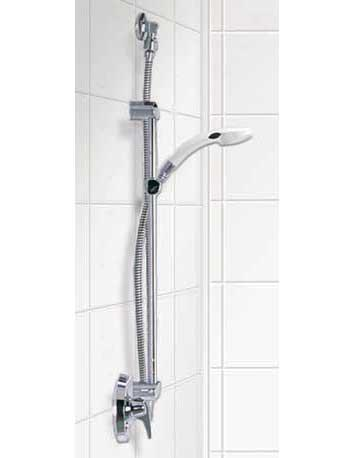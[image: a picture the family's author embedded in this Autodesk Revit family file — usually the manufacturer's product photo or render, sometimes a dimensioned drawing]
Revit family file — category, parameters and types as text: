
# Revit family: 13636FHARFR-L
name_source: partatom
category: Plumbing Fixtures
units: mm (PartAtom-declared; Revit-internal decimal feet)

## family parameters
Always vertical = Yes
Cut with Voids When Loaded = No
OmniClass Number = 23.45.00.00
OmniClass Title = Sanitary, Laundry, and Cleaning Equipment
Part Type = Normal
Room Calculation Point = No
Round Connector Dimension = Use Diameter
Shared = No
Work Plane-Based = No

## types (2) — shared parameters
Assembly Code = D2010710
Back Wall Thickness = 1 1/2"
Center of Shower = 19 1/4"
Default Elevation = 0"
Depth = 39 3/8"
Description = 62"W x 33"D COMPRESSION-MOLDED  SOLID  SURFACE  SHOWER  BASE W/ TRENCH DRAIN
Drain = 3 1/4"
Drain Offset Side = 19 1/4"
Drain Offset Wall = 19 1/4"
Grab Bars = Steel-Comfort Designs Bathware-304-Stainless Steel
Height = 78 1/4"
Keynote = COMPRESSION-MOLDED  SOLID  SURFACE  SHOWER  BASE W/ TRENCH DRAIN
Length = 38 1/2"
Manufacturer = Comfort Designs
MasterFormat Number = 22.42.23
MasterFormat Title = Commercial Showers
Model = SWB6234TR.75
Nailing Flange = 3/4"
OmniClass Number = 23.45.05.14.11.21
OmniClass Title = Shower Receptors
Part Thickness = 1/4"
S Bar Level = 34 5/8"
Seat Finish = Steel-Comfort Designs Bathware-304-Stainless Steel
Seat Level = 18 5/8"
Side Wall Thickness = 1 1/2"
Smooth Gelcoat = Gelcoat-Asura-White
Trench drain material = Drain
URL = http://www.comfortdesignsbathware.com

## per-type parameters (varying)
| type | Left Flange | Right Flange |
| 13636FHARFR | No | Yes |
| 13636FHARFL | Yes | No |

## geometry (parser evidence)
native form markers: Blend x6, Sweep x19
no freeform markers — native parametric forms only
